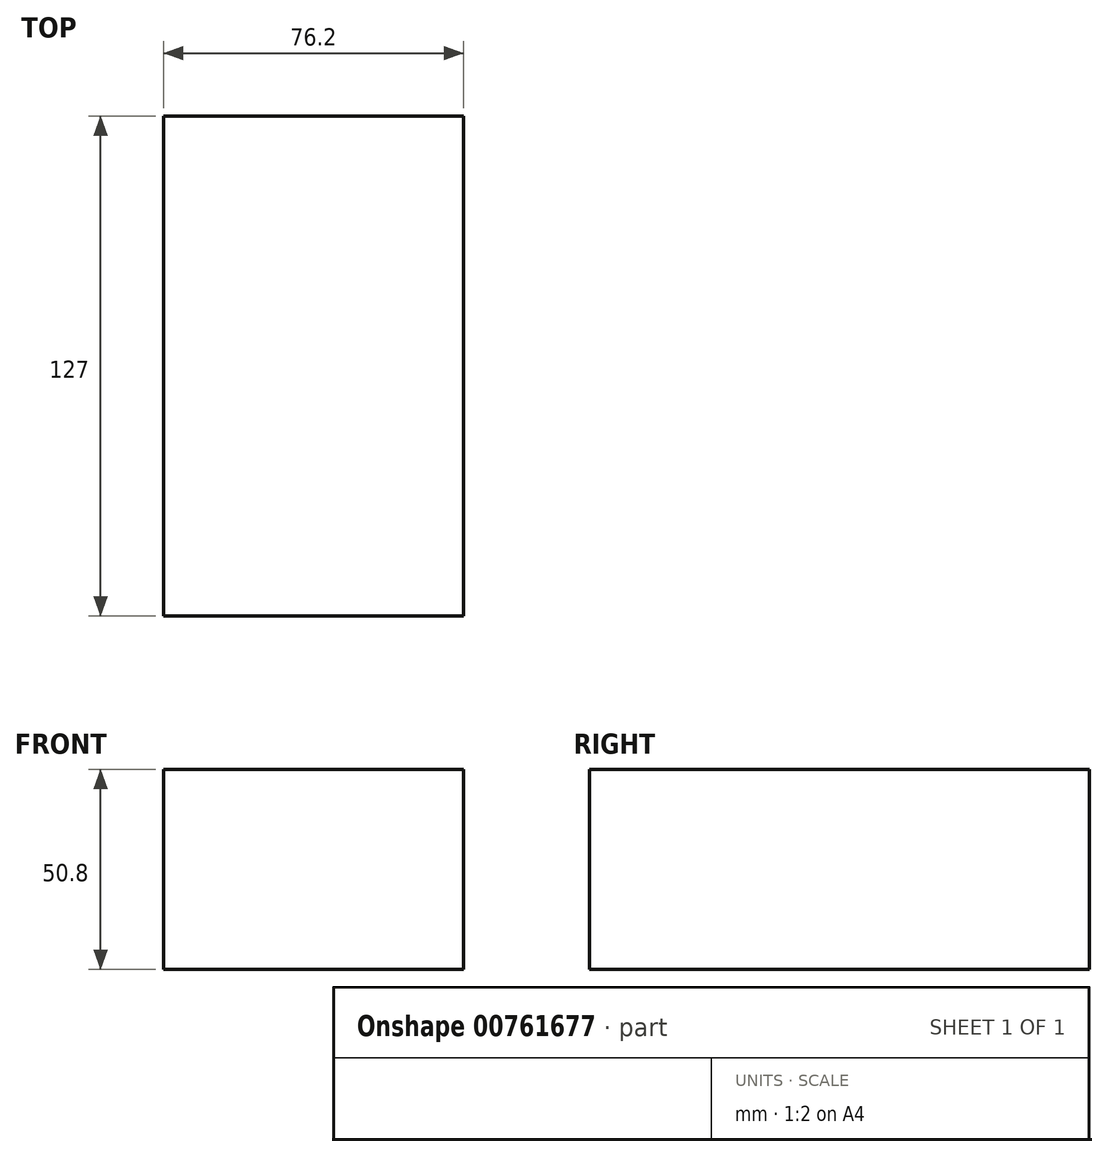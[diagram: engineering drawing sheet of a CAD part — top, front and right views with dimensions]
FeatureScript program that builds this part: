
annotation { "Feature Type Name" : "Feature", "Feature Type Description" : "" }
export const myFeature = defineFeature(function(context is Context, id is Id, definition is map)
    precondition{}
    {
        {
            var Q0;
            Q0=qCreatedBy(makeId("Front.planeOp"),FACE);
            var sketch = newSketch(context, id + "F0", { "sketchPlane" : qUnion([Q0])});
            skLineSegment(sketch, "E0.bottom", {"start": v(0, 0) * mm, "end": v(76.2, 0) * mm});
            skLineSegment(sketch, "E0.top", {"start": v(0, 50.8) * mm, "end": v(76.2, 50.8) * mm});
            skLineSegment(sketch, "E0.left", {"start": v(0, 0) * mm, "end": v(0, 50.8) * mm});
            skLineSegment(sketch, "E0.right", {"start": v(76.2, 0) * mm, "end": v(76.2, 50.8) * mm});
            skSolve(sketch);
        }
        {
            var Q0;
            Q0 = qSketchRegion(id + "F0", true);
            extrude(context, id + "F1", {"entities" : qUnion([Q0]), "depth" : 127 * mm, "offsetDistance" : 25.4 * mm});
        }
    });
